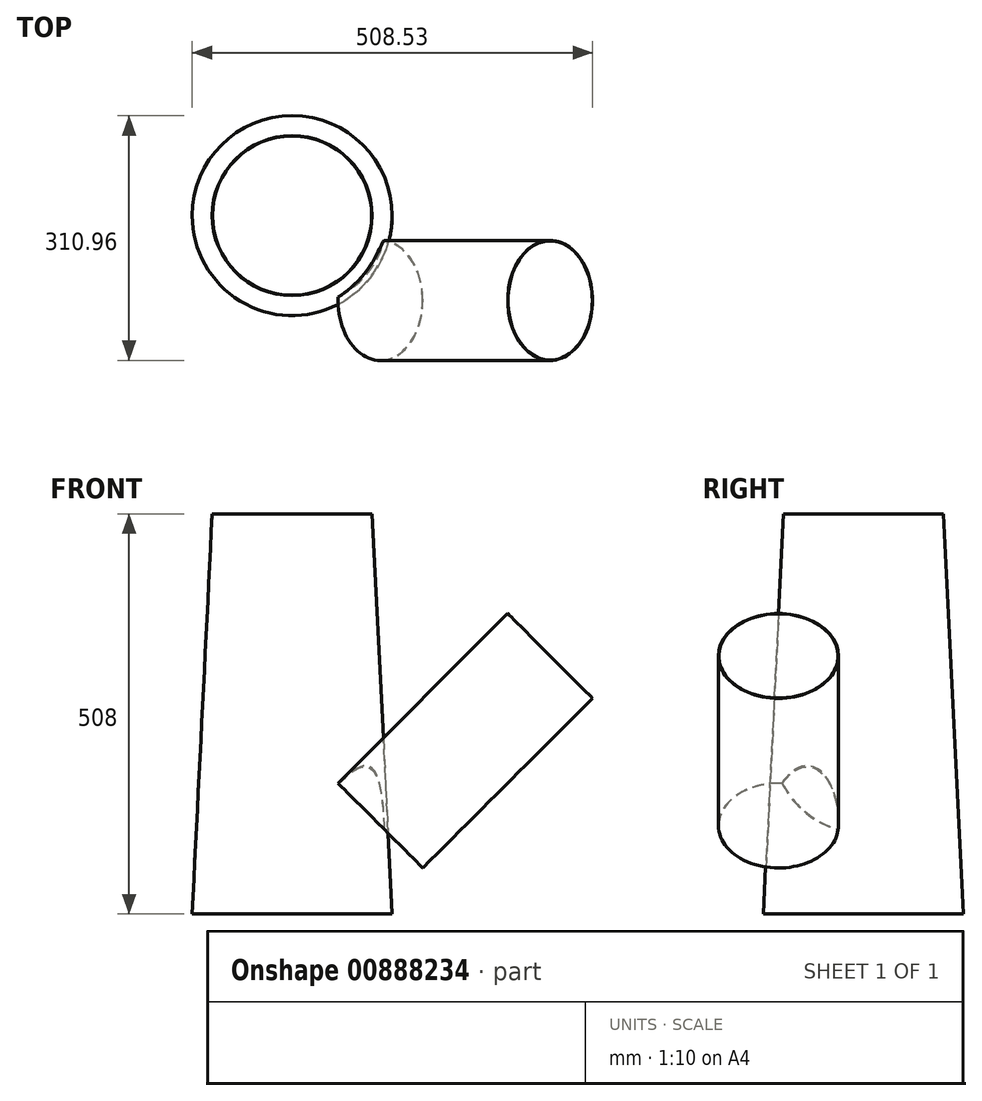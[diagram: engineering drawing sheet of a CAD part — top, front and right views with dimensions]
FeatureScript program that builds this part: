
annotation { "Feature Type Name" : "Feature", "Feature Type Description" : "" }
export const myFeature = defineFeature(function(context is Context, id is Id, definition is map)
    precondition{}
    {
        {
            var Q0;
            Q0=qCreatedBy(makeId("Front.planeOp"),FACE);
            var sketch = newSketch(context, id + "F0", { "sketchPlane" : qUnion([Q0])});
            skLineSegment(sketch, "E0", {"start": v(0, 0) * mm, "end": v(0, 508) * mm});
            skLineSegment(sketch, "E1", {"start": v(0, 508) * mm, "end": v(0, 254) * mm});
            skLineSegment(sketch, "E2", {"start": v(0, 152.4) * mm, "end": v(251.45, 403.85) * mm});
            skPoint(sketch, "E3", {"position": v(251.45, 403.85) * mm});
            skSolve(sketch);
        }
        {
            var Q0;
            Q0=sQuery(id+"F0.wireOp",VERTEX,"E0.start");
            var Q1;
            Q1=sQuery(id+"F0.wireOp",EDGE,"E0");
            cPlane(context, id + "F1", {"entities" : qUnion([Q0, Q1]), "cplaneType" : CPlaneType.LINE_POINT, "offset" : 25.4 * mm, "width" : 152.4 * mm, "height" : 152.4 * mm});
        }
        {
            var Q0;
            Q0=sQuery(id+"F0.wireOp",VERTEX,"E0.end");
            var Q1;
            Q1=sQuery(id+"F0.wireOp",EDGE,"E1");
            cPlane(context, id + "F2", {"entities" : qUnion([Q0, Q1]), "cplaneType" : CPlaneType.LINE_POINT, "offset" : 25.4 * mm, "width" : 152.4 * mm, "height" : 152.4 * mm});
        }
        {
            var Q0;
            Q0=sQuery(id+"F0.wireOp",VERTEX,"E2.end");
            var Q1;
            Q1=sQuery(id+"F0.wireOp",EDGE,"E2");
            cPlane(context, id + "F3", {"entities" : qUnion([Q0, Q1]), "cplaneType" : CPlaneType.LINE_POINT, "offset" : 25.4 * mm, "width" : 152.4 * mm, "height" : 152.4 * mm});
        }
        {
            var Q0;
            Q0=qCreatedBy(id+"F1.planeOp",FACE);
            var sketch = newSketch(context, id + "F4", { "sketchPlane" : qUnion([Q0])});
            skCircle(sketch, "E4", {"center": v(0, 0) * mm, "radius": 127 * mm});
            skSolve(sketch);
        }
        {
            var Q0;
            Q0=qCreatedBy(id+"F2.planeOp",FACE);
            var sketch = newSketch(context, id + "F5", { "sketchPlane" : qUnion([Q0])});
            skCircle(sketch, "E5", {"center": v(0, 0) * mm, "radius": 101.6 * mm});
            skSolve(sketch);
        }
        {
            var Q0;
            Q0=makeQuery(id+"F5.imprint","IMPRINT",FACE,{"disambiguationData":[TD([[makeQuery(id+"F5.imprint","IMPRINT",EDGE,{"derivedFrom":sQuery(id+"F5.wireOp",EDGE,"E5")}),1.0]])]});
            var Q1;
            Q1=makeQuery(id+"F4.imprint","IMPRINT",FACE,{"disambiguationData":[TD([[makeQuery(id+"F4.imprint","IMPRINT",EDGE,{"derivedFrom":sQuery(id+"F4.wireOp",EDGE,"E4")}),1.0]])]});
            var Q2;
            Q2=sQuery(id+"F4.wireOp",EDGE,"E4");
            var Q3;
            Q3=sQuery(id+"F5.wireOp",EDGE,"E5");
            loft(context, id + "F6", {"sheetProfilesArray" : [{ "sheetProfileEntities" : qUnion([Q0]) }, { "sheetProfileEntities" : qUnion([Q1]) }], "wireProfilesArray" : [{ "wireProfileEntities" : qUnion([Q2]) }, { "wireProfileEntities" : qUnion([Q3]) }]});
        }
        {
            var Q0;
            Q0=qCreatedBy(id+"F3.planeOp",FACE);
            var sketch = newSketch(context, id + "F7", { "sketchPlane" : qUnion([Q0])});
            skPoint(sketch, "E6", {"position": v(-107.76, 0) * mm});
            skCircle(sketch, "E7", {"center": v(-107.76, 0) * mm, "radius": 76.2 * mm});
            skSolve(sketch);
        }
        {
            var Q0;
            Q0=makeQuery(id+"F7.imprint","IMPRINT",FACE,{"disambiguationData":[TD([[makeQuery(id+"F7.imprint","IMPRINT",EDGE,{"derivedFrom":sQuery(id+"F7.wireOp",EDGE,"E7")}),1.0]])]});
            extrude(context, id + "F8", {"entities" : qUnion([Q0]), "operationType" : NewBodyOperationType.ADD, "oppositeDirection" : true, "depth" : 304.8 * mm, "offsetDistance" : 25.4 * mm});
        }
        {
            var Q0;
            Q0=qCreatedBy(id+"F3.planeOp",FACE);
            var sketch = newSketch(context, id + "F9", { "sketchPlane" : qUnion([Q0])});
            skCircle(sketch, "E8", {"center": v(-107.76, 0) * mm, "radius": 75.72 * mm});
            skSolve(sketch);
        }
        {
            var Q0;
            Q0 = qSketchRegion(id + "F9", true);
            extrude(context, id + "F10", {"entities" : qUnion([Q0]), "operationType" : NewBodyOperationType.REMOVE, "oppositeDirection" : true, "depth" : 304.8 * mm, "offsetDistance" : 25.4 * mm});
        }
        {
            var Q0;
            Q0=makeQuery(id+"F6.opLoft","CAP_FACE",FACE,{"disambiguationData":[OSD([makeQuery(id+"F4.imprint","IMPRINT",FACE,{"disambiguationData":[TD([[makeQuery(id+"F4.imprint","IMPRINT",EDGE,{"derivedFrom":sQuery(id+"F4.wireOp",EDGE,"E4")}),1.0]])]})])],"isStart":true});
            var sketch = newSketch(context, id + "F11", { "sketchPlane" : qUnion([Q0])});
            skCircle(sketch, "E9", {"center": v(0, 0) * mm, "radius": 126.52 * mm});
            skSolve(sketch);
        }
        {
            var Q0;
            Q0=makeQuery(id+"F6.opLoft","CAP_FACE",FACE,{"disambiguationData":[OSD([makeQuery(id+"F5.imprint","IMPRINT",FACE,{"disambiguationData":[TD([[makeQuery(id+"F5.imprint","IMPRINT",EDGE,{"derivedFrom":sQuery(id+"F5.wireOp",EDGE,"E5")}),1.0]])]})])],"isStart":true});
            var sketch = newSketch(context, id + "F12", { "sketchPlane" : qUnion([Q0])});
            skCircle(sketch, "E10", {"center": v(0, 0) * mm, "radius": 101.12 * mm});
            skSolve(sketch);
        }
        {
            var Q1;
            Q1 = qSketchRegion(id + "F11", true);
            var Q2;
            Q2 = qSketchRegion(id + "F12", true);
            loft(context, id + "F13", {"operationType" : NewBodyOperationType.REMOVE, "sheetProfilesArray" : [{ "sheetProfileEntities" : qUnion([Q1]) }, { "sheetProfileEntities" : qUnion([Q2]) }]});
        }
    });
